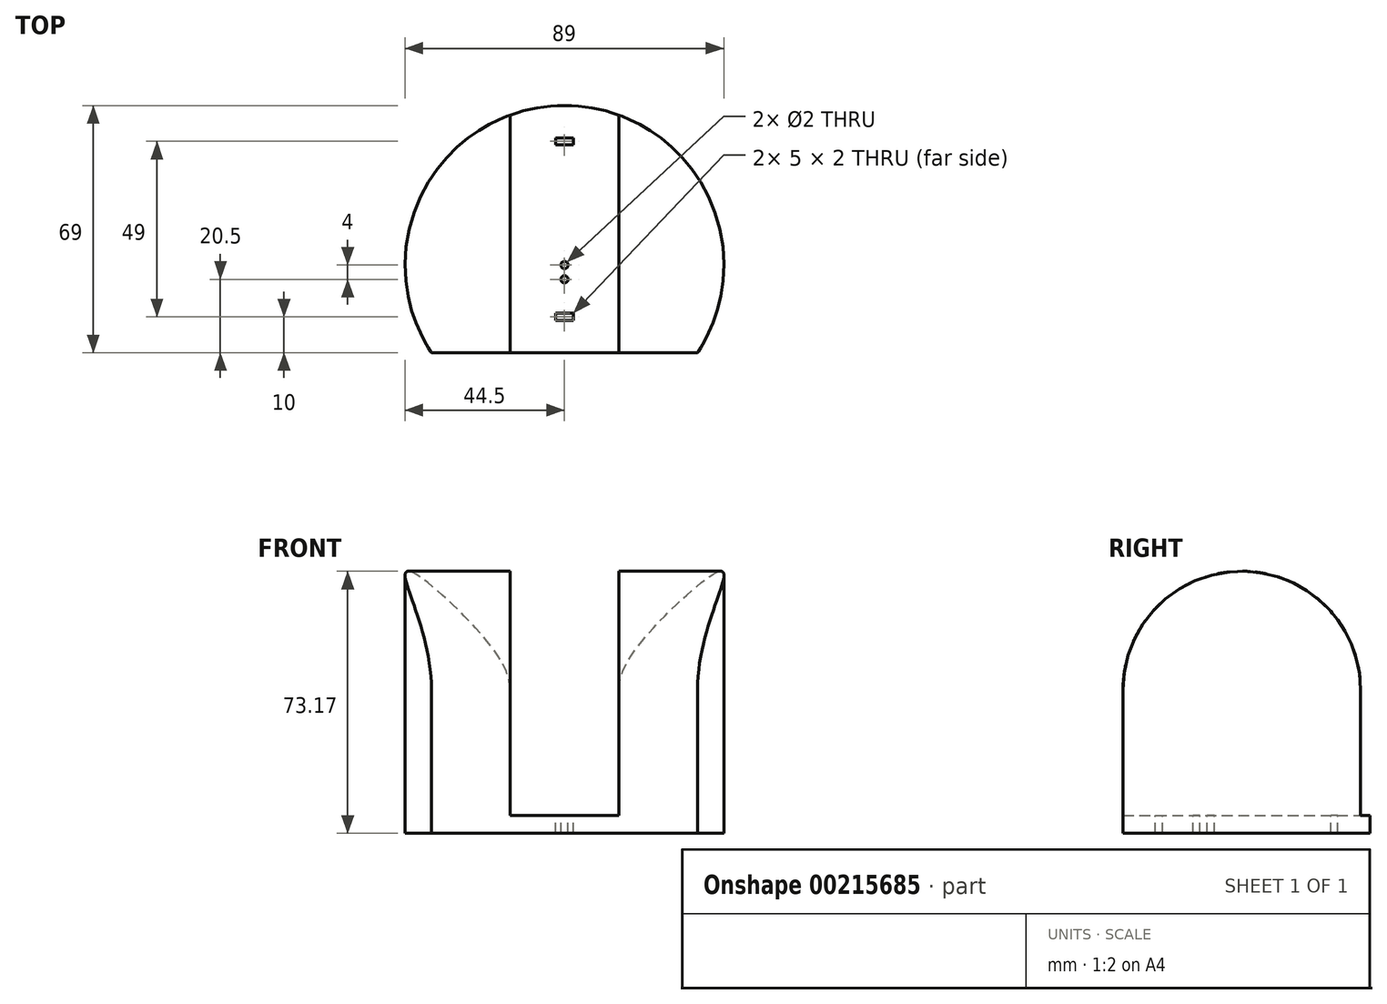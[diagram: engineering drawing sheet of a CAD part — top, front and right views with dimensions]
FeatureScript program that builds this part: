
annotation { "Feature Type Name" : "Feature", "Feature Type Description" : "" }
export const myFeature = defineFeature(function(context is Context, id is Id, definition is map)
    precondition{}
    {
        {
            var Q0;
            Q0=qCreatedBy(makeId("Top.planeOp"),FACE);
            var sketch = newSketch(context, id + "F0", { "sketchPlane" : qUnion([Q0])});
            skArc(sketch, "E0", {"start": v(-37.15, -24.5) * mm, "mid": v(0, 44.5) * mm, "end": v(37.15, -24.5) * mm});
            skLineSegment(sketch, "E1", {"start": v(-37.15, -24.5) * mm, "end": v(37.15, -24.5) * mm});
            skArc(sketch, "E2", {"start": v(-31.94, -15.5) * mm, "mid": v(0, 35.5) * mm, "end": v(31.94, -15.5) * mm, "construction": true});
            skLineSegment(sketch, "E3", {"start": v(-31.94, -15.5) * mm, "end": v(31.94, -15.5) * mm, "construction": true});
            skSolve(sketch);
        }
        {
            var Q0;
            Q0 = qSketchRegion(id + "F0", true);
            extrude(context, id + "F1", {"entities" : qUnion([Q0]), "depth" : 5 * mm});
        }
        {
            var Q0;
            Q0=makeQuery(id+"F1.opExtrude","CAP_FACE",FACE,{"disambiguationData":[OSD([sQuery(id+"F0.wireOp",EDGE,"E0"),sQuery(id+"F0.wireOp",EDGE,"E1")])],"isStart":false});
            var sketch = newSketch(context, id + "F2", { "sketchPlane" : qUnion([Q0])});
            skLineSegment(sketch, "E4", {"start": v(-37.15, -24.5) * mm, "end": v(-15.15, -24.5) * mm});
            skLineSegment(sketch, "E5", {"start": v(-15.15, -24.5) * mm, "end": v(-15.15, 41.84) * mm});
            skArc(sketch, "E6", {"start": v(-15.15, 41.84) * mm, "mid": v(-42.24, 14) * mm, "end": v(-37.15, -24.5) * mm});
            skLineSegment(sketch, "E7.MirrorCS", {"start": v(15.15, -24.5) * mm, "end": v(15.15, 41.84) * mm});
            skArc(sketch, "E8.MirrorCS", {"start": v(15.15, 41.84) * mm, "mid": v(42.24, 14) * mm, "end": v(37.15, -24.5) * mm});
            skLineSegment(sketch, "E9.MirrorCS", {"start": v(37.15, -24.5) * mm, "end": v(15.15, -24.5) * mm});
            skSolve(sketch);
        }
        {
            var Q0;
            Q0 = qSketchRegion(id + "F2", true);
            extrude(context, id + "F3", {"entities" : qUnion([Q0]), "operationType" : NewBodyOperationType.ADD, "depth" : 70 * mm});
        }
        {
            var Q0;
            Q0=makeQuery(id+"F3.opExtrude","SWEPT_FACE",FACE,{"disambiguationData":[OSD([sQuery(id+"F2.wireOp",EDGE,"E5")])]});
            var sketch = newSketch(context, id + "F4", { "sketchPlane" : qUnion([Q0])});
            skArc(sketch, "E10", {"start": v(41.84, 40) * mm, "mid": v(8.67, 73.17) * mm, "end": v(-24.5, 40) * mm});
            skLineSegment(sketch, "E11", {"start": v(-24.5, 40) * mm, "end": v(41.84, 40) * mm, "construction": true});
            skLineSegment(sketch, "E12", {"start": v(-24.5, 40) * mm, "end": v(-45.5, 40) * mm});
            skLineSegment(sketch, "E13", {"start": v(-45.5, 40) * mm, "end": v(-45.5, 90) * mm});
            skLineSegment(sketch, "E14", {"start": v(-45.5, 90) * mm, "end": v(58.5, 90) * mm});
            skLineSegment(sketch, "E15", {"start": v(58.5, 90) * mm, "end": v(58.5, 40) * mm});
            skLineSegment(sketch, "E16", {"start": v(58.5, 40) * mm, "end": v(41.84, 40) * mm});
            skSolve(sketch);
        }
        {
            var Q0;
            Q0 = qSketchRegion(id + "F4", true);
            var Q1;
            Q1 = qConstructionFilter(qBodyType(qCreatedBy(id + "F4" ,EDGE), BodyType.WIRE), ConstructionObject.NO);
            extrude(context, id + "F5", {"entities" : qUnion([Q0]), "operationType" : NewBodyOperationType.REMOVE, "surfaceEntities" : qUnion([Q1]), "endBound" : BoundingType.THROUGH_ALL, "oppositeDirection" : true, "depth" : 25 * mm});
        }
        {
            var Q0;
            Q0 = qSketchRegion(id + "F4", true);
            extrude(context, id + "F6", {"entities" : qUnion([Q0]), "operationType" : NewBodyOperationType.REMOVE, "endBound" : BoundingType.THROUGH_ALL, "depth" : 25 * mm});
        }
        {
            var Q0;
            Q0=makeQuery(id+"F1.opExtrude","CAP_FACE",FACE,{"disambiguationData":[OSD([sQuery(id+"F0.wireOp",EDGE,"E0"),sQuery(id+"F0.wireOp",EDGE,"E1")])],"isStart":false});
            var sketch = newSketch(context, id + "F7", { "sketchPlane" : qUnion([Q0])});
            skCircle(sketch, "E17", {"center": v(0, 0) * mm, "radius": 33.5 * mm, "construction": true});
            skLineSegment(sketch, "E18", {"start": v(0, 0) * mm, "end": v(0, 33.5) * mm, "construction": true});
            skLineSegment(sketch, "E19", {"start": v(0, 33.5) * mm, "end": v(-2.5, 33.5) * mm});
            skLineSegment(sketch, "E20", {"start": v(-2.5, 33.5) * mm, "end": v(-2.5, 35.5) * mm});
            skLineSegment(sketch, "E21", {"start": v(-2.5, 35.5) * mm, "end": v(2.5, 35.5) * mm});
            skLineSegment(sketch, "E22", {"start": v(2.5, 35.5) * mm, "end": v(2.5, 33.5) * mm});
            skLineSegment(sketch, "E23", {"start": v(2.5, 33.5) * mm, "end": v(0, 33.5) * mm});
            skPoint(sketch, "E24.endSnap0", {"position": v(0, -24.5) * mm});
            skLineSegment(sketch, "E25.bottom", {"start": v(-2.5, -15.5) * mm, "end": v(2.5, -15.5) * mm});
            skLineSegment(sketch, "E25.top", {"start": v(-2.5, -13.5) * mm, "end": v(2.5, -13.5) * mm});
            skLineSegment(sketch, "E25.left", {"start": v(-2.5, -15.5) * mm, "end": v(-2.5, -13.5) * mm});
            skLineSegment(sketch, "E25.right", {"start": v(2.5, -15.5) * mm, "end": v(2.5, -13.5) * mm});
            skSolve(sketch);
        }
        {
            var Q0;
            Q0 = qSketchRegion(id + "F7", true);
            extrude(context, id + "F8", {"entities" : qUnion([Q0]), "operationType" : NewBodyOperationType.REMOVE, "endBound" : BoundingType.THROUGH_ALL, "oppositeDirection" : true, "depth" : 25 * mm});
        }
        {
            var Q0;
            Q0=makeQuery(id+"F1.opExtrude","CAP_FACE",FACE,{"disambiguationData":[OSD([sQuery(id+"F0.wireOp",EDGE,"E0"),sQuery(id+"F0.wireOp",EDGE,"E1")])],"isStart":false});
            var sketch = newSketch(context, id + "F9", { "sketchPlane" : qUnion([Q0])});
            skCircle(sketch, "E26", {"center": v(0, 0) * mm, "radius": 1 * mm});
            skCircle(sketch, "E27", {"center": v(0, -4) * mm, "radius": 1 * mm});
            skSolve(sketch);
        }
        {
            var Q0;
            Q0 = qSketchRegion(id + "F9", true);
            extrude(context, id + "F10", {"entities" : qUnion([Q0]), "operationType" : NewBodyOperationType.REMOVE, "endBound" : BoundingType.THROUGH_ALL, "oppositeDirection" : true, "depth" : 25 * mm});
        }
    });
